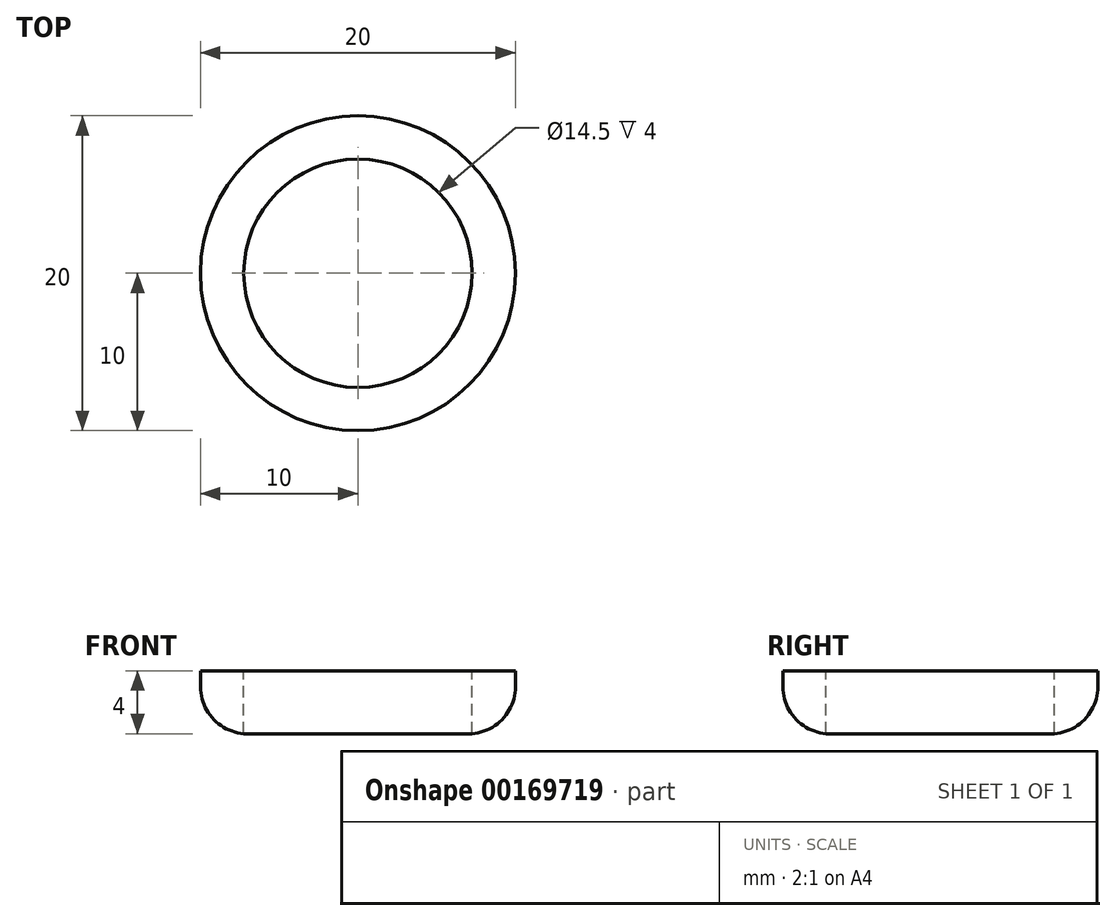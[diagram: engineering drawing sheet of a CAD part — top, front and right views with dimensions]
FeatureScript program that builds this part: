
annotation { "Feature Type Name" : "Feature", "Feature Type Description" : "" }
export const myFeature = defineFeature(function(context is Context, id is Id, definition is map)
    precondition{}
    {
        {
            var Q0;
            Q0=qCreatedBy(makeId("Top.planeOp"),FACE);
            var sketch = newSketch(context, id + "F0", { "sketchPlane" : qUnion([Q0])});
            skCircle(sketch, "E0", {"center": v(0, 0) * mm, "radius": 10 * mm});
            skCircle(sketch, "E1", {"center": v(0, 0) * mm, "radius": 7.25 * mm});
            skSolve(sketch);
        }
        {
            var Q0;
            Q0 = qSketchRegion(id + "F0", true);
            extrude(context, id + "F1", {"entities" : qUnion([Q0]), "oppositeDirection" : true, "depth" : 4 * mm});
        }
        {
            var Q0;
            Q0=makeQuery(id+"F1.opExtrude","CAP_EDGE",EDGE,{"disambiguationData":[OSD([sQuery(id+"F0.wireOp",EDGE,"E0")])],"isStart":false});
            fillet(context, id + "F2", {"entities" : qUnion([Q0]), "radius" : 3 * mm, "tangentPropagation" : true, "allowEdgeOverflow" : false});
        }
    });
